# Revit family: Нагреватель электрический круглый E
name_source: partatom
category: Арматура воздуховодов
units: mm (PartAtom-declared; Revit-internal decimal feet)

## family parameters
Всегда вертикально = Да
На основе рабочей плоскости = Нет
Общий = Нет
При загрузке вырезать с полостями = Нет
Размер круглого соединителя = Использовать диаметр
Тип детали = Вставляется

## types (6) — shared parameters
ADSK_Единица измерения = шт.
ADSK_Завод-изготовитель = Naveka
ADSK_Наименование = Воздухонагреватель электрический для круглого канала
Материал = RAL 0000 Серый металл
Таблица = Электронагреватель Е

## per-type parameters (varying)
| type | ADSK_Марка | B | D | H | L | d | d+5 | d1 | h1 | Масса, кг | Мощность нагревателя N,кВт | Ток, А | Требуемая мощность, кВт | Фазность |
| E...-250 | E2-250 | 255 мм | 250 мм | 350 мм | 250 мм | 245 мм | 250 мм | 125 мм | 143 мм | 3,4 | 2 | 9,1 | 2 мм | 1 |
| E...-100 | E1-100 | 105 мм | 100 мм | 200 мм | 250 мм | 95 мм | 100 мм | 50 мм | 68 мм | 1,7 | 1 | 4,5 | 1 мм | 1 |
| E...-125 | E1-125 | 130 мм | 125 мм | 225 мм | 250 мм | 120 мм | 125 мм | 63 мм | 81 мм | 1,9 | 1 | 4,5 | 1 мм | 1 |
| E...-160 | E3-160 | 165 мм | 160 мм | 260 мм | 250 мм | 155 мм | 160 мм | 80 мм | 98 мм | 2,6 | 3 | 6,8 | 3 мм | 1 |
| E...-200 | E4,5-200 | 205 мм | 200 мм | 300 мм | 300 мм | 195 мм | 200 мм | 100 мм | 118 мм | 3,5 | 4,5 | 6,8 | 5 мм | 3 |
| E...-315 | E3-315 | 320 мм | 315 мм | 415 мм | 250 мм | 310 мм | 315 мм | 158 мм | 176 мм | 4,2 | 3 | 13,6 | 3 мм | 1 |
